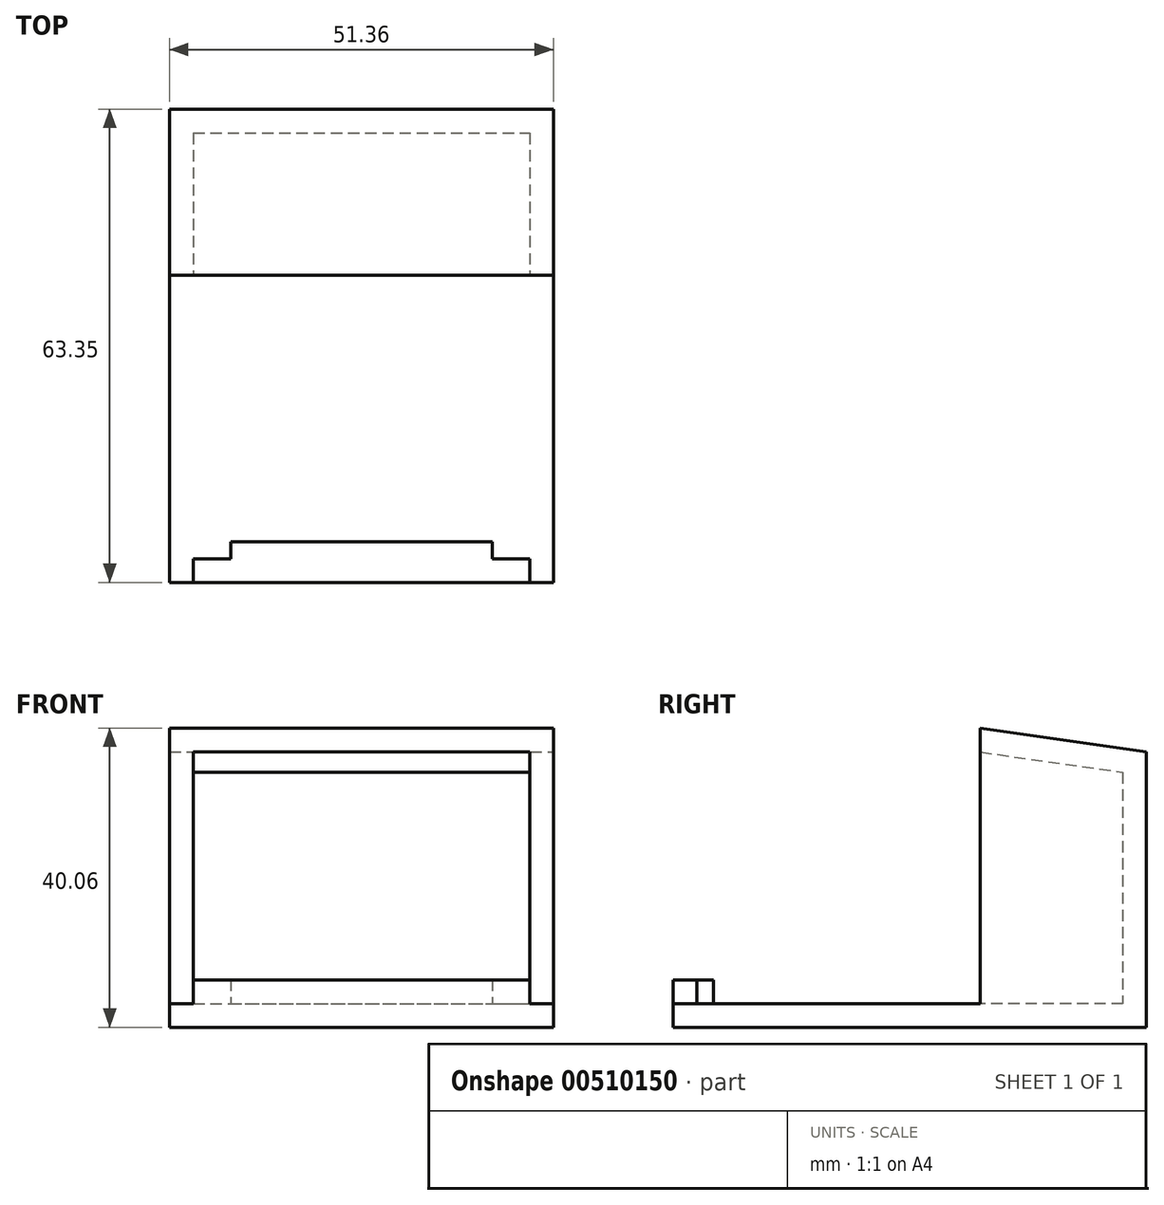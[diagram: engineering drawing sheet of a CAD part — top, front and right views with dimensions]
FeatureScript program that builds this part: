
annotation { "Feature Type Name" : "Feature", "Feature Type Description" : "" }
export const myFeature = defineFeature(function(context is Context, id is Id, definition is map)
    precondition{}
    {
        {
            var Q0;
            Q0=qCreatedBy(makeId("Top.planeOp"),FACE);
            var sketch = newSketch(context, id + "F0", { "sketchPlane" : qUnion([Q0])});
            skLineSegment(sketch, "E0", {"start": v(0, 0) * mm, "end": v(45, 0) * mm});
            skLineSegment(sketch, "E1", {"start": v(22.5, 0) * mm, "end": v(22.5, -54.75) * mm});
            skLineSegment(sketch, "E2", {"start": v(5, -54.75) * mm, "end": v(40, -54.75) * mm});
            skLineSegment(sketch, "E3", {"start": v(45, 0) * mm, "end": v(45, -57) * mm});
            skLineSegment(sketch, "E4", {"start": v(0, 0) * mm, "end": v(0, -57) * mm});
            skLineSegment(sketch, "E5", {"start": v(5, -54.75) * mm, "end": v(5, -57) * mm});
            skLineSegment(sketch, "E6", {"start": v(0, -57) * mm, "end": v(5, -57) * mm});
            skLineSegment(sketch, "E7", {"start": v(40, -54.75) * mm, "end": v(40, -57) * mm});
            skLineSegment(sketch, "E8.trimOffspring", {"start": v(40, -57) * mm, "end": v(45, -57) * mm});
            skLineSegment(sketch, "E9.2", {"start": v(48.17, 3.18) * mm, "end": v(48.18, -60.18) * mm});
            skLineSegment(sketch, "E9.3", {"start": v(-3.18, 3.18) * mm, "end": v(48.18, 3.18) * mm});
            skLineSegment(sketch, "E9.4", {"start": v(-3.18, 3.18) * mm, "end": v(-3.17, -60.17) * mm});
            skLineSegment(sketch, "E10", {"start": v(-3.17, -60.18) * mm, "end": v(48.18, -60.18) * mm});
            skSolve(sketch);
        }
        {
            var Q0;
            {var subQ1=sQuery(id+"F0.wireOp",EDGE,"E1");Q0=makeQuery(id+"F0.imprint","IMPRINT",FACE,{"disambiguationData":[TD([[makeQuery(id+"F0.imprint","IMPRINT",EDGE,{"derivedFrom":subQ1}),-1.0]])]});}
            var Q1;
            {var subQ1=sQuery(id+"F0.wireOp",EDGE,"E1");Q1=makeQuery(id+"F0.imprint","IMPRINT",FACE,{"disambiguationData":[TD([[makeQuery(id+"F0.imprint","IMPRINT",EDGE,{"derivedFrom":subQ1}),1.0]])]});}
            var Q2;
            {var subQ3=sQuery(id+"F0.wireOp",EDGE,"E3");Q2=makeQuery(id+"F0.imprint","IMPRINT",FACE,{"disambiguationData":[TD([[makeQuery(id+"F0.imprint","IMPRINT",EDGE,{"derivedFrom":subQ3}),1.0]])]});}
            extrude(context, id + "F1", {"entities" : qUnion([Q0, Q1, Q2]), "depth" : 3.17 * mm, "offsetDistance" : 25.4 * mm});
        }
        {
            var Q0;
            Q0=makeQuery(id+"F1.opExtrude","CAP_FACE",FACE,{"disambiguationData":[OSD([sQuery(id+"F0.wireOp",EDGE,"E9.2"),sQuery(id+"F0.wireOp",EDGE,"E9.3"),sQuery(id+"F0.wireOp",EDGE,"E9.4"),sQuery(id+"F0.wireOp",EDGE,"E10")])],"isStart":false});
            var sketch = newSketch(context, id + "F2", { "sketchPlane" : qUnion([Q0])});
            skLineSegment(sketch, "E11", {"start": v(0, 0) * mm, "end": v(45, 0) * mm});
            skLineSegment(sketch, "E12", {"start": v(22.5, 0) * mm, "end": v(22.5, -54.75) * mm});
            skLineSegment(sketch, "E13", {"start": v(5, -54.75) * mm, "end": v(40, -54.75) * mm});
            skLineSegment(sketch, "E14", {"start": v(45, 0) * mm, "end": v(45, -57) * mm});
            skLineSegment(sketch, "E15", {"start": v(0, 0) * mm, "end": v(0, -57) * mm});
            skLineSegment(sketch, "E16", {"start": v(5, -54.75) * mm, "end": v(5, -57) * mm});
            skLineSegment(sketch, "E17", {"start": v(0, -57) * mm, "end": v(5, -57) * mm});
            skLineSegment(sketch, "E18", {"start": v(40, -54.75) * mm, "end": v(40, -57) * mm});
            skLineSegment(sketch, "E19.trimOffspring", {"start": v(40, -57) * mm, "end": v(45, -57) * mm});
            skLineSegment(sketch, "E20.2", {"start": v(48.17, 3.18) * mm, "end": v(48.18, -60.18) * mm});
            skLineSegment(sketch, "E20.3", {"start": v(-3.18, 3.18) * mm, "end": v(48.18, 3.18) * mm});
            skLineSegment(sketch, "E20.4", {"start": v(-3.17, 3.18) * mm, "end": v(-3.17, -60.17) * mm});
            skLineSegment(sketch, "E21", {"start": v(-3.17, -60.18) * mm, "end": v(48.18, -60.18) * mm});
            skLineSegment(sketch, "E22", {"start": v(0, 0) * mm, "end": v(0, -19.05) * mm});
            skLineSegment(sketch, "E23", {"start": v(0, -19.05) * mm, "end": v(-3.17, -19.05) * mm});
            skLineSegment(sketch, "E24", {"start": v(45, 0) * mm, "end": v(45, -19.05) * mm});
            skLineSegment(sketch, "E25", {"start": v(45, -19.05) * mm, "end": v(48.17, -19.05) * mm});
            skSolve(sketch);
        }
        {
            var Q0;
            {var subQ8=sQuery(id+"F2.wireOp",EDGE,"E20.3");Q0=makeQuery(id+"F2.imprint","IMPRINT",FACE,{"disambiguationData":[TD([[makeQuery(id+"F2.imprint","IMPRINT",EDGE,{"derivedFrom":subQ8}),-1.0]])]});}
            extrude(context, id + "F3", {"entities" : qUnion([Q0]), "operationType" : NewBodyOperationType.ADD, "depth" : 30.5 * mm, "offsetDistance" : 25.4 * mm});
        }
        {
            var Q0;
            Q0=makeQuery(id+"F3.boolean.opBoolean","MERGE",FACE,{"derivedFrom":[makeQuery(id+"F1.opExtrude","SWEPT_FACE",FACE,{"disambiguationData":[OSD([sQuery(id+"F0.wireOp",EDGE,"E9.2")])]}),makeQuery(id+"F3.opExtrude","SWEPT_FACE",FACE,{"disambiguationData":[OSD([sQuery(id+"F2.wireOp",EDGE,"E20.2")])]})]});
            var sketch = newSketch(context, id + "F4", { "sketchPlane" : qUnion([Q0])});
            skLineSegment(sketch, "E26", {"start": v(-19.05, 33.67) * mm, "end": v(-19.05, 36.85) * mm});
            skLineSegment(sketch, "E27", {"start": v(-19.05, 36.85) * mm, "end": v(3.17, 33.67) * mm});
            skLineSegment(sketch, "E28.0", {"start": v(-19.05, 40.06) * mm, "end": v(3.18, 36.88) * mm});
            skLineSegment(sketch, "E29", {"start": v(-19.05, 36.85) * mm, "end": v(-19.05, 40.06) * mm});
            skLineSegment(sketch, "E30", {"start": v(3.17, 33.67) * mm, "end": v(3.17, 36.88) * mm});
            skSolve(sketch);
        }
        {
            var Q0;
            Q0=makeQuery(id+"F4.imprint","IMPRINT",FACE,{"disambiguationData":[TD([[makeQuery(id+"F4.imprint","IMPRINT",EDGE,{"derivedFrom":sQuery(id+"F4.wireOp",EDGE,"E26")}),-1.0]])]});
            var Q1;
            Q1=makeQuery(id+"F4.imprint","IMPRINT",FACE,{"disambiguationData":[TD([[makeQuery(id+"F4.imprint","IMPRINT",EDGE,{"derivedFrom":sQuery(id+"F4.wireOp",EDGE,"E27")}),1.0]])]});
            var Q2;
            Q2=makeQuery(id+"F3.opExtrude","SWEPT_FACE",FACE,{"disambiguationData":[OSD([sQuery(id+"F2.wireOp",EDGE,"E14")])]});
            extrude(context, id + "F5", {"entities" : qUnion([Q0, Q1]), "operationType" : NewBodyOperationType.ADD, "endBound" : BoundingType.UP_TO_SURFACE, "oppositeDirection" : true, "depth" : 25.4 * mm, "endBoundEntityFace" : qUnion([Q2]), "offsetDistance" : 25.4 * mm});
        }
        {
            var Q0;
            Q0=makeQuery(id+"F3.boolean.opBoolean","MERGE",FACE,{"derivedFrom":[makeQuery(id+"F1.opExtrude","SWEPT_FACE",FACE,{"disambiguationData":[OSD([sQuery(id+"F0.wireOp",EDGE,"E9.4")])]}),makeQuery(id+"F3.opExtrude","SWEPT_FACE",FACE,{"disambiguationData":[OSD([sQuery(id+"F2.wireOp",EDGE,"E20.4")])]})]});
            var sketch = newSketch(context, id + "F6", { "sketchPlane" : qUnion([Q0])});
            skLineSegment(sketch, "E31", {"start": v(19.05, 33.67) * mm, "end": v(19.05, 36.85) * mm});
            skLineSegment(sketch, "E32", {"start": v(19.05, 36.85) * mm, "end": v(19.05, 40.06) * mm});
            skLineSegment(sketch, "E33.MirrorCS", {"start": v(-3.18, 33.67) * mm, "end": v(-3.18, 36.88) * mm});
            skLineSegment(sketch, "E34.MirrorCS", {"start": v(19.05, 36.85) * mm, "end": v(-3.18, 33.67) * mm});
            skLineSegment(sketch, "E35.MirrorCS", {"start": v(19.05, 40.06) * mm, "end": v(-3.18, 36.88) * mm});
            skSolve(sketch);
        }
        {
            var Q0;
            Q0 = qSketchRegion(id + "F6", true);
            var Q1;
            Q1=makeQuery(id+"F6.imprint","IMPRINT",FACE,{"disambiguationData":[TD([[makeQuery(id+"F6.imprint","IMPRINT",EDGE,{"derivedFrom":sQuery(id+"F6.wireOp",EDGE,"E31")}),1.0]])]});
            var Q2;
            Q2=makeQuery(id+"F3.opExtrude","SWEPT_FACE",FACE,{"disambiguationData":[OSD([sQuery(id+"F2.wireOp",EDGE,"E15")])]});
            extrude(context, id + "F7", {"entities" : qUnion([Q0, Q1]), "operationType" : NewBodyOperationType.ADD, "endBound" : BoundingType.UP_TO_SURFACE, "oppositeDirection" : true, "depth" : 25.4 * mm, "endBoundEntityFace" : qUnion([Q2]), "offsetDistance" : 25.4 * mm});
        }
        {
            var Q0;
            Q0=makeQuery(id+"F7.boolean.opBoolean","MERGE",FACE,{"derivedFrom":[makeQuery(id+"F3.opExtrude","SWEPT_FACE",FACE,{"disambiguationData":[OSD([sQuery(id+"F2.wireOp",EDGE,"E15")])]}),makeQuery(id+"F7.opExtrude","CAP_FACE",FACE,{"disambiguationData":[OSD([sQuery(id+"F2.wireOp",EDGE,"E20.4"),sQuery(id+"F6.wireOp",EDGE,"E31"),sQuery(id+"F6.wireOp",EDGE,"E32"),sQuery(id+"F6.wireOp",EDGE,"E33.MirrorCS"),sQuery(id+"F6.wireOp",EDGE,"E35.MirrorCS")])],"isStart":false})]});
            var sketch = newSketch(context, id + "F8", { "sketchPlane" : qUnion([Q0])});
            skLineSegment(sketch, "E36", {"start": v(-19.05, 33.67) * mm, "end": v(-19.05, 36.85) * mm});
            skLineSegment(sketch, "E37", {"start": v(-19.05, 36.85) * mm, "end": v(0, 34.13) * mm});
            skLineSegment(sketch, "E38.0", {"start": v(-19.05, 40.06) * mm, "end": v(3.18, 36.88) * mm});
            skLineSegment(sketch, "E39", {"start": v(-19.05, 36.85) * mm, "end": v(-19.05, 40.06) * mm});
            skLineSegment(sketch, "E40", {"start": v(3.18, 33.67) * mm, "end": v(3.18, 36.88) * mm});
            skLineSegment(sketch, "E41", {"start": v(0, 33.67) * mm, "end": v(0, 34.13) * mm});
            skSolve(sketch);
        }
        {
            var Q0;
            Q0 = qSketchRegion(id + "F8", true);
            var Q1;
            Q1=makeQuery(id+"F8.imprint","IMPRINT",FACE,{"disambiguationData":[TD([[makeQuery(id+"F8.imprint","IMPRINT",EDGE,{"derivedFrom":sQuery(id+"F8.wireOp",EDGE,"E37")}),1.0]])]});
            var Q2;
            Q2=makeQuery(id+"F5.boolean.opBoolean","MERGE",FACE,{"derivedFrom":[makeQuery(id+"F3.opExtrude","SWEPT_FACE",FACE,{"disambiguationData":[OSD([sQuery(id+"F2.wireOp",EDGE,"E14")])]}),makeQuery(id+"F5.opExtrude","CAP_FACE",FACE,{"disambiguationData":[OSD([sQuery(id+"F2.wireOp",EDGE,"E20.2"),sQuery(id+"F4.wireOp",EDGE,"E26"),sQuery(id+"F4.wireOp",EDGE,"E28.0"),sQuery(id+"F4.wireOp",EDGE,"E29"),sQuery(id+"F4.wireOp",EDGE,"E30")])],"isStart":false})]});
            extrude(context, id + "F9", {"entities" : qUnion([Q0, Q1]), "operationType" : NewBodyOperationType.ADD, "endBound" : BoundingType.UP_TO_SURFACE, "depth" : 25.4 * mm, "endBoundEntityFace" : qUnion([Q2]), "offsetDistance" : 25.4 * mm});
        }
        {
            var Q0;
            Q0=makeQuery(id+"F1.opExtrude","CAP_FACE",FACE,{"disambiguationData":[OSD([sQuery(id+"F0.wireOp",EDGE,"E9.2"),sQuery(id+"F0.wireOp",EDGE,"E9.3"),sQuery(id+"F0.wireOp",EDGE,"E9.4"),sQuery(id+"F0.wireOp",EDGE,"E10")])],"isStart":false});
            var sketch = newSketch(context, id + "F10", { "sketchPlane" : qUnion([Q0])});
            skLineSegment(sketch, "E42", {"start": v(0, 0) * mm, "end": v(45, 0) * mm});
            skLineSegment(sketch, "E43", {"start": v(22.5, 0) * mm, "end": v(22.5, -54.75) * mm});
            skLineSegment(sketch, "E44", {"start": v(5, -54.75) * mm, "end": v(40, -54.75) * mm});
            skLineSegment(sketch, "E45", {"start": v(45, 0) * mm, "end": v(45, -57) * mm});
            skLineSegment(sketch, "E46", {"start": v(0, 0) * mm, "end": v(0, -57) * mm});
            skLineSegment(sketch, "E47", {"start": v(5, -54.75) * mm, "end": v(5, -57) * mm});
            skLineSegment(sketch, "E48", {"start": v(0, -57) * mm, "end": v(5, -57) * mm});
            skLineSegment(sketch, "E49", {"start": v(40, -54.75) * mm, "end": v(40, -57) * mm});
            skLineSegment(sketch, "E50.trimOffspring", {"start": v(40, -57) * mm, "end": v(45, -57) * mm});
            skLineSegment(sketch, "E51.2", {"start": v(48.17, 3.17) * mm, "end": v(48.18, -60.18) * mm});
            skLineSegment(sketch, "E51.3", {"start": v(-3.18, 3.17) * mm, "end": v(48.18, 3.17) * mm});
            skLineSegment(sketch, "E51.4", {"start": v(-3.18, 3.17) * mm, "end": v(-3.17, -60.18) * mm});
            skLineSegment(sketch, "E52", {"start": v(-3.17, -60.18) * mm, "end": v(48.18, -60.18) * mm});
            skLineSegment(sketch, "E53", {"start": v(0, -57) * mm, "end": v(0, -68.94) * mm});
            skLineSegment(sketch, "E54", {"start": v(45, -57) * mm, "end": v(45, -72.8) * mm});
            skSolve(sketch);
        }
        {
            var Q0;
            {var subQ4=sQuery(id+"F10.wireOp",EDGE,"E47");Q0=makeQuery(id+"F10.imprint","IMPRINT",FACE,{"disambiguationData":[TD([[makeQuery(id+"F10.imprint","IMPRINT",EDGE,{"derivedFrom":subQ4}),1.0]])]});}
            extrude(context, id + "F11", {"entities" : qUnion([Q0]), "operationType" : NewBodyOperationType.ADD, "depth" : 3.17 * mm, "offsetDistance" : 25.4 * mm});
        }
    });
